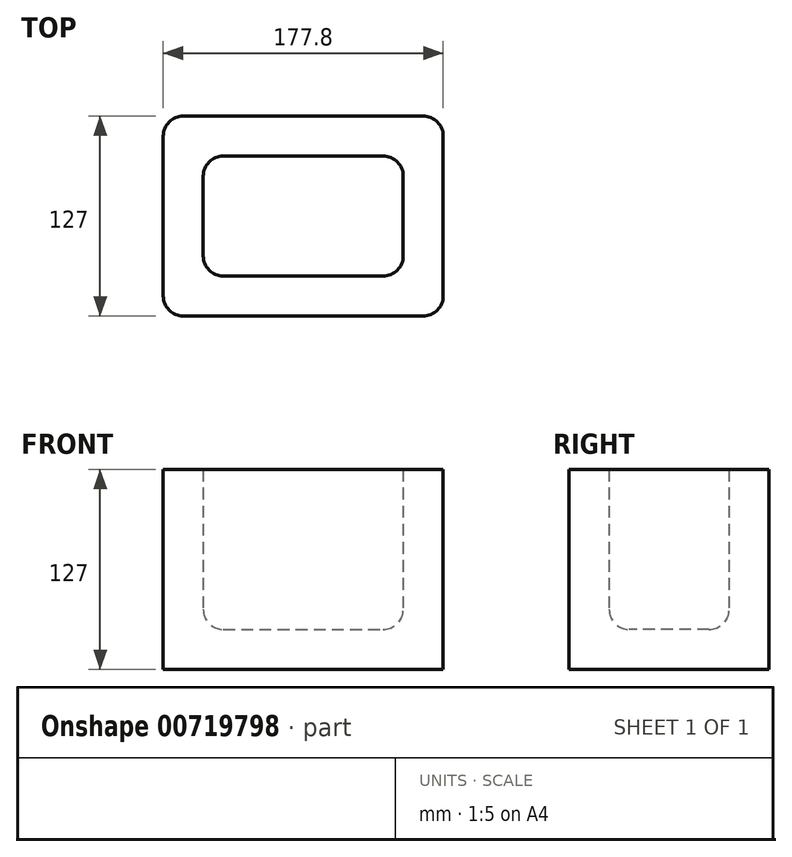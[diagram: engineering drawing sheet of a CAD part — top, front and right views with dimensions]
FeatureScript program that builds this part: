
annotation { "Feature Type Name" : "Feature", "Feature Type Description" : "" }
export const myFeature = defineFeature(function(context is Context, id is Id, definition is map)
    precondition{}
    {
        {
            var Q0;
            Q0=qCreatedBy(makeId("Top.planeOp"),FACE);
            var sketch = newSketch(context, id + "F0", { "sketchPlane" : qUnion([Q0])});
            skLineSegment(sketch, "E0.bottom", {"start": v(0, 0) * mm, "end": v(177.8, 0) * mm});
            skLineSegment(sketch, "E0.top", {"start": v(0, -127) * mm, "end": v(177.8, -127) * mm});
            skLineSegment(sketch, "E0.left", {"start": v(0, 0) * mm, "end": v(0, -127) * mm});
            skLineSegment(sketch, "E0.right", {"start": v(177.8, 0) * mm, "end": v(177.8, -127) * mm});
            skSolve(sketch);
        }
        {
            var Q0;
            Q0 = qSketchRegion(id + "F0", true);
            extrude(context, id + "F1", {"entities" : qUnion([Q0]), "depth" : 127 * mm, "offsetDistance" : 25.4 * mm});
        }
        {
            var Q0;
            Q0=makeQuery(id+"F1.opExtrude","CAP_FACE",FACE,{"disambiguationData":[OSD([sQuery(id+"F0.wireOp",EDGE,"E0.bottom"),sQuery(id+"F0.wireOp",EDGE,"E0.top"),sQuery(id+"F0.wireOp",EDGE,"E0.left"),sQuery(id+"F0.wireOp",EDGE,"E0.right")])],"isStart":false});
            shell(context, id + "F2", {"entities" : qUnion([Q0]), "thickness" : 25.4 * mm});
        }
        {
            var Q0;
            Q0=makeQuery(id+"F2.opShell","OFFSET_EDGE",EDGE,{"disambiguationData":[OSD([sQuery(id+"F0.wireOp",EDGE,"E0.top"),sQuery(id+"F0.wireOp",EDGE,"E0.right")])]});
            var Q1;
            {var subQ0=sQuery(id+"F0.wireOp",EDGE,"E0.top");Q1=makeQuery(id+"F2.opShell","OFFSET_EDGE",EDGE,{"disambiguationData":[OSD([subQ0]),TDD([makeQuery(id+"F1.opExtrude","CAP_EDGE",EDGE,{"disambiguationData":[OSD([subQ0])],"isStart":true})])]});}
            var Q2;
            Q2=makeQuery(id+"F2.opShell","OFFSET_EDGE",EDGE,{"disambiguationData":[OSD([sQuery(id+"F0.wireOp",EDGE,"E0.top"),sQuery(id+"F0.wireOp",EDGE,"E0.left")])]});
            var Q3;
            Q3=makeQuery(id+"F2.opShell","OFFSET_EDGE",EDGE,{"disambiguationData":[OSD([sQuery(id+"F0.wireOp",EDGE,"E0.bottom"),sQuery(id+"F0.wireOp",EDGE,"E0.left")])]});
            var Q4;
            {var subQ0=sQuery(id+"F0.wireOp",EDGE,"E0.left");Q4=makeQuery(id+"F2.opShell","OFFSET_EDGE",EDGE,{"disambiguationData":[OSD([subQ0]),TDD([makeQuery(id+"F1.opExtrude","CAP_EDGE",EDGE,{"disambiguationData":[OSD([subQ0])],"isStart":true})])]});}
            var Q5;
            {var subQ0=sQuery(id+"F0.wireOp",EDGE,"E0.bottom");Q5=makeQuery(id+"F2.opShell","OFFSET_EDGE",EDGE,{"disambiguationData":[OSD([subQ0]),TDD([makeQuery(id+"F1.opExtrude","CAP_EDGE",EDGE,{"disambiguationData":[OSD([subQ0])],"isStart":true})])]});}
            var Q6;
            Q6=makeQuery(id+"F2.opShell","OFFSET_EDGE",EDGE,{"disambiguationData":[OSD([sQuery(id+"F0.wireOp",EDGE,"E0.bottom"),sQuery(id+"F0.wireOp",EDGE,"E0.right")])]});
            var Q7;
            {var subQ0=sQuery(id+"F0.wireOp",EDGE,"E0.right");Q7=makeQuery(id+"F2.opShell","OFFSET_EDGE",EDGE,{"disambiguationData":[OSD([subQ0]),TDD([makeQuery(id+"F1.opExtrude","CAP_EDGE",EDGE,{"disambiguationData":[OSD([subQ0])],"isStart":true})])]});}
            var Q8;
            Q8=makeQuery(id+"F1.opExtrude","SWEPT_EDGE",EDGE,{"disambiguationData":[OSD([sQuery(id+"F0.wireOp",EDGE,"E0.bottom"),sQuery(id+"F0.wireOp",EDGE,"E0.right")])]});
            var Q9;
            Q9=makeQuery(id+"F1.opExtrude","SWEPT_EDGE",EDGE,{"disambiguationData":[OSD([sQuery(id+"F0.wireOp",EDGE,"E0.top"),sQuery(id+"F0.wireOp",EDGE,"E0.right")])]});
            var Q10;
            Q10=makeQuery(id+"F1.opExtrude","SWEPT_EDGE",EDGE,{"disambiguationData":[OSD([sQuery(id+"F0.wireOp",EDGE,"E0.top"),sQuery(id+"F0.wireOp",EDGE,"E0.left")])]});
            var Q11;
            Q11=makeQuery(id+"F1.opExtrude","SWEPT_EDGE",EDGE,{"disambiguationData":[OSD([sQuery(id+"F0.wireOp",EDGE,"E0.bottom"),sQuery(id+"F0.wireOp",EDGE,"E0.left")])]});
            fillet(context, id + "F3", {"entities" : qUnion([Q0, Q1, Q2, Q3, Q4, Q5, Q6, Q7, Q8, Q9, Q10, Q11]), "radius" : 12.7 * mm, "tangentPropagation" : true, "allowEdgeOverflow" : false});
        }
    });
